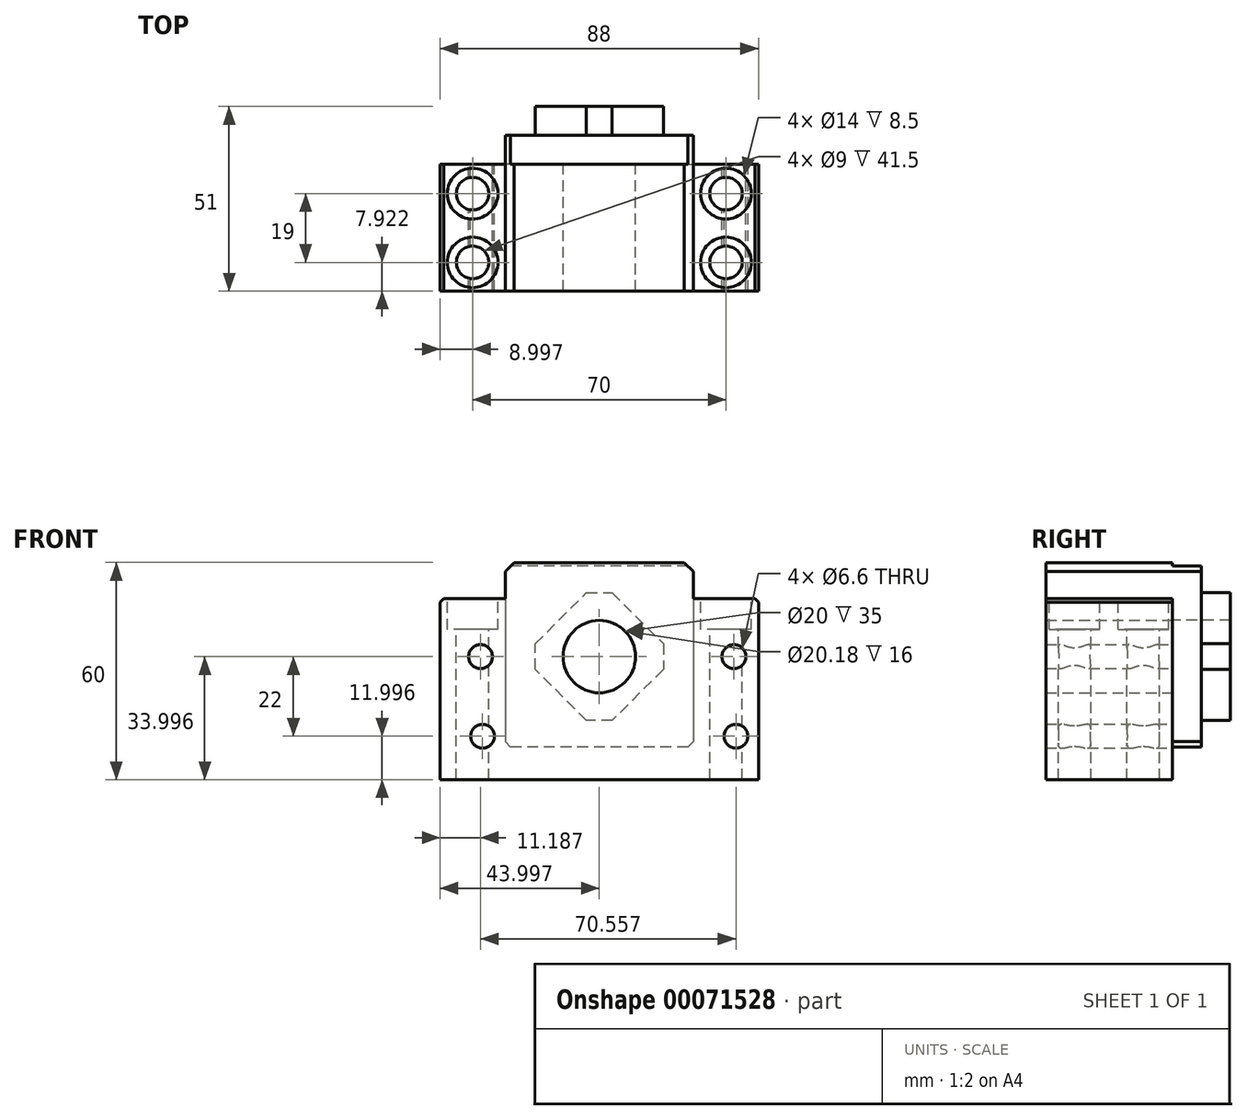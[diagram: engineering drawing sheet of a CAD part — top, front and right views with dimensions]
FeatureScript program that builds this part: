
annotation { "Feature Type Name" : "Feature", "Feature Type Description" : "" }
export const myFeature = defineFeature(function(context is Context, id is Id, definition is map)
    precondition{}
    {
        {
            var Q0;
            Q0=qCreatedBy(makeId("Front.planeOp"),FACE);
            var sketch = newSketch(context, id + "F0", { "sketchPlane" : qUnion([Q0])});
            skLineSegment(sketch, "E0.bottom", {"start": v(-37.23, 17.93) * mm, "end": v(-21.73, 17.93) * mm});
            skLineSegment(sketch, "E0.top", {"start": v(-39.73, -32.07) * mm, "end": v(48.27, -32.07) * mm});
            skLineSegment(sketch, "E0.left", {"start": v(-39.73, 15.43) * mm, "end": v(-39.73, -32.07) * mm});
            skLineSegment(sketch, "E0.right", {"start": v(48.27, 15.43) * mm, "end": v(48.27, -32.07) * mm});
            skCircle(sketch, "E1", {"center": v(4.27, 1.93) * mm, "radius": 10 * mm});
            skLineSegment(sketch, "E2.bottom", {"start": v(-21.73, 27.93) * mm, "end": v(30.27, 27.93) * mm});
            skLineSegment(sketch, "E2.left", {"start": v(-21.73, 27.93) * mm, "end": v(-21.73, 17.93) * mm});
            skLineSegment(sketch, "E2.right", {"start": v(30.27, 27.93) * mm, "end": v(30.27, 17.93) * mm});
            skLineSegment(sketch, "E3.trimOffspring", {"start": v(30.27, 17.93) * mm, "end": v(45.77, 17.93) * mm});
            skCircle(sketch, "E4", {"center": v(-28.54, 1.93) * mm, "radius": 3.3 * mm});
            skCircle(sketch, "E5", {"center": v(-27.99, -20.07) * mm, "radius": 3.3 * mm});
            skCircle(sketch, "E6", {"center": v(42.01, -20.07) * mm, "radius": 3.3 * mm});
            skCircle(sketch, "E7", {"center": v(41.46, 1.93) * mm, "radius": 3.3 * mm});
            skLineSegment(sketch, "E8.top", {"start": v(-39.73, 17.93) * mm, "end": v(-33.45, 17.93) * mm});
            skLineSegment(sketch, "E8.left", {"start": v(-39.73, 9.55) * mm, "end": v(-39.73, 17.93) * mm});
            skLineSegment(sketch, "E9.bottom", {"start": v(42.4, 17.93) * mm, "end": v(48.27, 17.93) * mm});
            skLineSegment(sketch, "E9.right", {"start": v(48.27, 17.93) * mm, "end": v(48.27, 11.22) * mm});
            skSolve(sketch);
        }
        {
            var Q0;
            {var subQ0=sQuery(id+"F0.wireOp",EDGE,"E0.bottom");Q0=makeQuery(id+"F0.imprint","IMPRINT",FACE,{"disambiguationData":[TD([[makeQuery(id+"F0.imprint","IMPRINT",EDGE,{"derivedFrom":subQ0}),-1.0]])]});}
            extrude(context, id + "F1", {"entities" : qUnion([Q0]), "depth" : 35 * mm});
        }
        {
            var Q0;
            Q0=makeQuery(id+"F1.opExtrude","SWEPT_EDGE",EDGE,{"disambiguationData":[OSD([sQuery(id+"F0.wireOp",EDGE,"E2.bottom"),sQuery(id+"F0.wireOp",EDGE,"E2.left")])]});
            var Q1;
            Q1=makeQuery(id+"F1.opExtrude","SWEPT_EDGE",EDGE,{"disambiguationData":[OSD([sQuery(id+"F0.wireOp",EDGE,"E2.bottom"),sQuery(id+"F0.wireOp",EDGE,"E2.right")])]});
            chamfer(context, id + "F2", {"entities" : qUnion([Q0, Q1]), "width" : 2.5 * mm, "tangentPropagation" : true});
        }
        {
            var Q0;
            Q0=makeQuery(id+"F1.opExtrude","SWEPT_FACE",FACE,{"disambiguationData":[OSD([sQuery(id+"F0.wireOp",EDGE,"E0.bottom")])]});
            var sketch = newSketch(context, id + "F3", { "sketchPlane" : qUnion([Q0])});
            skCircle(sketch, "E10", {"center": v(39.27, -27.08) * mm, "radius": 7 * mm});
            skCircle(sketch, "E11", {"center": v(-30.73, -8.08) * mm, "radius": 4.5 * mm});
            skCircle(sketch, "E12", {"center": v(39.27, -8.08) * mm, "radius": 7 * mm});
            skCircle(sketch, "E13", {"center": v(39.27, -27.08) * mm, "radius": 4.5 * mm});
            skCircle(sketch, "E14", {"center": v(-30.73, -27.08) * mm, "radius": 4.5 * mm});
            skCircle(sketch, "E15", {"center": v(39.27, -8.08) * mm, "radius": 4.5 * mm});
            skCircle(sketch, "E16", {"center": v(-30.73, -8.08) * mm, "radius": 7 * mm});
            skCircle(sketch, "E17", {"center": v(-30.73, -27.08) * mm, "radius": 7 * mm});
            skSolve(sketch);
        }
        {
            var Q0;
            Q0=makeQuery(id+"F3.imprint","IMPRINT",FACE,{"disambiguationData":[TD([[makeQuery(id+"F3.imprint","IMPRINT",EDGE,{"derivedFrom":sQuery(id+"F3.wireOp",EDGE,"E10")}),1.0]])]});
            var Q1;
            Q1=makeQuery(id+"F3.imprint","IMPRINT",FACE,{"disambiguationData":[TD([[makeQuery(id+"F3.imprint","IMPRINT",EDGE,{"derivedFrom":sQuery(id+"F3.wireOp",EDGE,"E12")}),1.0]])]});
            var Q2;
            Q2=makeQuery(id+"F3.imprint","IMPRINT",FACE,{"disambiguationData":[TD([[makeQuery(id+"F3.imprint","IMPRINT",EDGE,{"derivedFrom":sQuery(id+"F3.wireOp",EDGE,"E11")}),-1.0]])]});
            var Q3;
            Q3=makeQuery(id+"F3.imprint","IMPRINT",FACE,{"disambiguationData":[TD([[makeQuery(id+"F3.imprint","IMPRINT",EDGE,{"derivedFrom":sQuery(id+"F3.wireOp",EDGE,"E14")}),-1.0]])]});
            extrude(context, id + "F4", {"entities" : qUnion([Q0, Q1, Q2, Q3]), "operationType" : NewBodyOperationType.REMOVE, "oppositeDirection" : true, "depth" : 8.5 * mm});
        }
        {
            var Q0;
            Q0=makeQuery(id+"F4.boolean.opBoolean","SPLIT",FACE,{"disambiguationData":[TD([makeQuery(id+"F4.opExtrude","SWEPT_FACE",FACE,{"disambiguationData":[OSD([sQuery(id+"F3.wireOp",EDGE,"E13")])]})])],"derivedFrom":makeQuery(id+"F1.opExtrude","SWEPT_FACE",FACE,{"disambiguationData":[OSD([sQuery(id+"F0.wireOp",EDGE,"E3.trimOffspring"),sQuery(id+"F0.wireOp",EDGE,"E9.bottom")])]})});
            var Q1;
            Q1=makeQuery(id+"F4.boolean.opBoolean","SPLIT",FACE,{"disambiguationData":[TD([makeQuery(id+"F4.opExtrude","SWEPT_FACE",FACE,{"disambiguationData":[OSD([sQuery(id+"F3.wireOp",EDGE,"E15")])]})])],"derivedFrom":makeQuery(id+"F1.opExtrude","SWEPT_FACE",FACE,{"disambiguationData":[OSD([sQuery(id+"F0.wireOp",EDGE,"E3.trimOffspring"),sQuery(id+"F0.wireOp",EDGE,"E9.bottom")])]})});
            var Q2;
            Q2=makeQuery(id+"F4.boolean.opBoolean","SPLIT",FACE,{"disambiguationData":[TD([makeQuery(id+"F4.opExtrude","SWEPT_FACE",FACE,{"disambiguationData":[OSD([sQuery(id+"F3.wireOp",EDGE,"E11")])]})])],"derivedFrom":makeQuery(id+"F1.opExtrude","SWEPT_FACE",FACE,{"disambiguationData":[OSD([sQuery(id+"F0.wireOp",EDGE,"E0.bottom"),sQuery(id+"F0.wireOp",EDGE,"E8.top")])]})});
            var Q3;
            Q3=makeQuery(id+"F4.boolean.opBoolean","SPLIT",FACE,{"disambiguationData":[TD([makeQuery(id+"F4.opExtrude","SWEPT_FACE",FACE,{"disambiguationData":[OSD([sQuery(id+"F3.wireOp",EDGE,"E14")])]})])],"derivedFrom":makeQuery(id+"F1.opExtrude","SWEPT_FACE",FACE,{"disambiguationData":[OSD([sQuery(id+"F0.wireOp",EDGE,"E0.bottom"),sQuery(id+"F0.wireOp",EDGE,"E8.top")])]})});
            extrude(context, id + "F5", {"entities" : qUnion([Q0, Q1, Q2, Q3]), "operationType" : NewBodyOperationType.REMOVE, "endBound" : BoundingType.THROUGH_ALL, "oppositeDirection" : true, "depth" : 25 * mm});
        }
        {
            var Q0;
            Q0=makeQuery(id+"F1.opExtrude","SWEPT_EDGE",EDGE,{"disambiguationData":[OSD([sQuery(id+"F0.wireOp",EDGE,"E9.bottom"),sQuery(id+"F0.wireOp",EDGE,"E9.right")])]});
            var Q1;
            Q1=makeQuery(id+"F1.opExtrude","SWEPT_EDGE",EDGE,{"disambiguationData":[OSD([sQuery(id+"F0.wireOp",EDGE,"E8.top"),sQuery(id+"F0.wireOp",EDGE,"E8.left")])]});
            chamfer(context, id + "F6", {"entities" : qUnion([Q0, Q1]), "width" : 1 * mm, "tangentPropagation" : true});
        }
        {
            var Q0;
            Q0=makeQuery(id+"F1.opExtrude","CAP_FACE",FACE,{"disambiguationData":[OSD([sQuery(id+"F0.wireOp",EDGE,"E0.bottom"),sQuery(id+"F0.wireOp",EDGE,"E0.top"),sQuery(id+"F0.wireOp",EDGE,"E0.left"),sQuery(id+"F0.wireOp",EDGE,"E0.right"),sQuery(id+"F0.wireOp",EDGE,"E1"),sQuery(id+"F0.wireOp",EDGE,"E2.bottom"),sQuery(id+"F0.wireOp",EDGE,"E2.left"),sQuery(id+"F0.wireOp",EDGE,"E2.right"),sQuery(id+"F0.wireOp",EDGE,"E3.trimOffspring"),sQuery(id+"F0.wireOp",EDGE,"E4"),sQuery(id+"F0.wireOp",EDGE,"E5"),sQuery(id+"F0.wireOp",EDGE,"E6"),sQuery(id+"F0.wireOp",EDGE,"E7"),sQuery(id+"F0.wireOp",EDGE,"E8.top"),sQuery(id+"F0.wireOp",EDGE,"E8.left"),sQuery(id+"F0.wireOp",EDGE,"E9.bottom"),sQuery(id+"F0.wireOp",EDGE,"E9.right")])],"isStart":true});
            var sketch = newSketch(context, id + "F7", { "sketchPlane" : qUnion([Q0])});
            skLineSegment(sketch, "E18.bottom", {"start": v(-30.27, 26.93) * mm, "end": v(21.73, 26.93) * mm});
            skLineSegment(sketch, "E18.top", {"start": v(-30.27, -23.07) * mm, "end": v(21.73, -23.07) * mm});
            skLineSegment(sketch, "E18.left", {"start": v(-30.27, 26.93) * mm, "end": v(-30.27, -23.07) * mm});
            skLineSegment(sketch, "E18.right", {"start": v(21.73, 26.93) * mm, "end": v(21.73, -23.07) * mm});
            skCircle(sketch, "E19", {"center": v(-4.27, 1.93) * mm, "radius": 10.09 * mm});
            skSolve(sketch);
        }
        {
            var Q0;
            Q0=qSketchRegion(id+"F7",true);
            extrude(context, id + "F8", {"entities" : qUnion([Q0]), "operationType" : NewBodyOperationType.ADD, "depth" : 8 * mm});
        }
        {
            var Q0;
            Q0=makeQuery(id+"F8.opExtrude","SWEPT_EDGE",EDGE,{"disambiguationData":[OSD([sQuery(id+"F7.wireOp",EDGE,"E18.bottom"),sQuery(id+"F7.wireOp",EDGE,"E18.left")])]});
            chamfer(context, id + "F9", {"entities" : qUnion([Q0]), "width" : 1.5 * mm, "tangentPropagation" : true});
        }
        {
            var Q0;
            Q0=makeQuery(id+"F8.opExtrude","SWEPT_EDGE",EDGE,{"disambiguationData":[OSD([sQuery(id+"F7.wireOp",EDGE,"E18.bottom"),sQuery(id+"F7.wireOp",EDGE,"E18.right")])]});
            var Q1;
            Q1=makeQuery(id+"F8.opExtrude","SWEPT_EDGE",EDGE,{"disambiguationData":[OSD([sQuery(id+"F7.wireOp",EDGE,"E18.top"),sQuery(id+"F7.wireOp",EDGE,"E18.left")])]});
            var Q2;
            Q2=makeQuery(id+"F8.opExtrude","SWEPT_EDGE",EDGE,{"disambiguationData":[OSD([sQuery(id+"F7.wireOp",EDGE,"E18.top"),sQuery(id+"F7.wireOp",EDGE,"E18.right")])]});
            chamfer(context, id + "F10", {"entities" : qUnion([Q0, Q1, Q2]), "width" : 1.5 * mm, "tangentPropagation" : true});
        }
        {
            var Q0;
            Q0=makeQuery(id+"F8.opExtrude","CAP_FACE",FACE,{"disambiguationData":[OSD([sQuery(id+"F7.wireOp",EDGE,"E18.bottom"),sQuery(id+"F7.wireOp",EDGE,"E18.top"),sQuery(id+"F7.wireOp",EDGE,"E18.left"),sQuery(id+"F7.wireOp",EDGE,"E18.right"),sQuery(id+"F7.wireOp",EDGE,"E19")])],"isStart":false});
            var sketch = newSketch(context, id + "F11", { "sketchPlane" : qUnion([Q0])});
            skLineSegment(sketch, "E20", {"start": v(-25.48, 1.93) * mm, "end": v(-4.27, -19.29) * mm});
            skLineSegment(sketch, "E21", {"start": v(-4.27, -19.29) * mm, "end": v(16.95, 1.93) * mm});
            skLineSegment(sketch, "E22", {"start": v(16.95, 1.93) * mm, "end": v(-4.27, 23.14) * mm});
            skLineSegment(sketch, "E23", {"start": v(-4.27, 23.14) * mm, "end": v(-25.48, 1.93) * mm});
            skSolve(sketch);
        }
        {
            var Q0;
            Q0=makeQuery(id+"F11.imprint","IMPRINT",FACE,{"disambiguationData":[TD([[makeQuery(id+"F11.imprint","IMPRINT",EDGE,{"derivedFrom":sQuery(id+"F11.wireOp",EDGE,"E20")}),1.0]])]});
            extrude(context, id + "F12", {"entities" : qUnion([Q0]), "operationType" : NewBodyOperationType.ADD, "depth" : 8 * mm});
        }
        {
            var Q0;
            Q0=makeQuery(id+"F12.opExtrude","SWEPT_EDGE",EDGE,{"disambiguationData":[OSD([sQuery(id+"F11.wireOp",EDGE,"E22"),sQuery(id+"F11.wireOp",EDGE,"E23")])]});
            var Q1;
            Q1=makeQuery(id+"F12.opExtrude","SWEPT_EDGE",EDGE,{"disambiguationData":[OSD([sQuery(id+"F11.wireOp",EDGE,"E20"),sQuery(id+"F11.wireOp",EDGE,"E23")])]});
            var Q2;
            Q2=makeQuery(id+"F12.opExtrude","SWEPT_EDGE",EDGE,{"disambiguationData":[OSD([sQuery(id+"F11.wireOp",EDGE,"E20"),sQuery(id+"F11.wireOp",EDGE,"E21")])]});
            var Q3;
            Q3=makeQuery(id+"F12.opExtrude","SWEPT_EDGE",EDGE,{"disambiguationData":[OSD([sQuery(id+"F11.wireOp",EDGE,"E21"),sQuery(id+"F11.wireOp",EDGE,"E22")])]});
            chamfer(context, id + "F13", {"entities" : qUnion([Q0, Q1, Q2, Q3]), "width" : 5 * mm, "tangentPropagation" : true});
        }
    });
